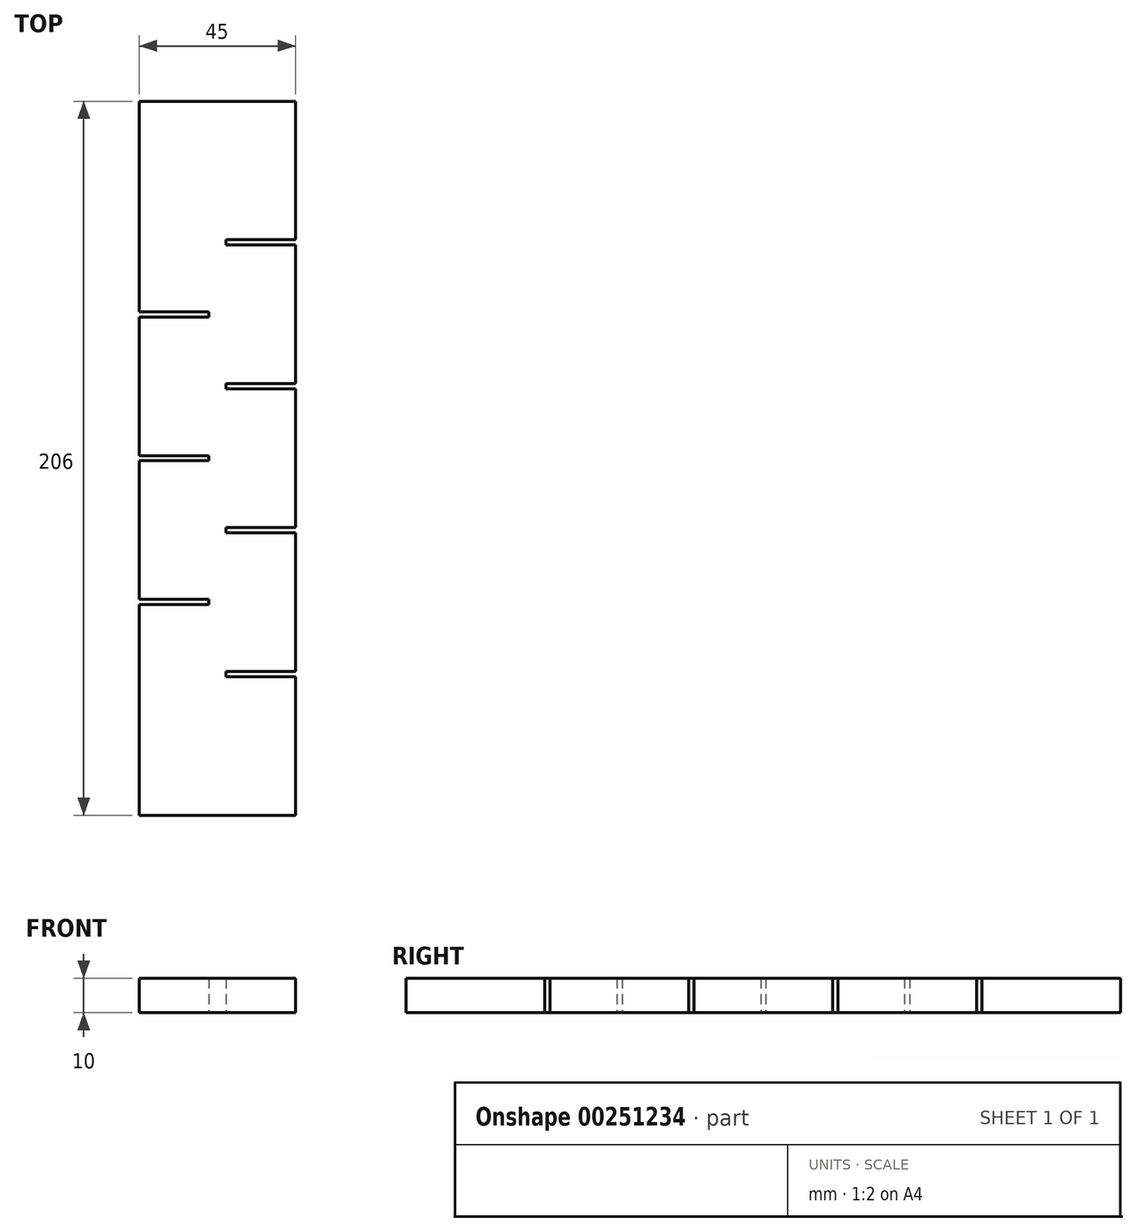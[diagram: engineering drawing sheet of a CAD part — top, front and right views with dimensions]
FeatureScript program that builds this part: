
annotation { "Feature Type Name" : "Feature", "Feature Type Description" : "" }
export const myFeature = defineFeature(function(context is Context, id is Id, definition is map)
    precondition{}
    {
        {
            var Q0;
            Q0=qCreatedBy(makeId("Top.planeOp"),FACE);
            var sketch = newSketch(context, id + "F0", { "sketchPlane" : qUnion([Q0])});
            skLineSegment(sketch, "E0", {"start": v(0, 0) * mm, "end": v(45, 0) * mm});
            skLineSegment(sketch, "E1", {"start": v(45, 0) * mm, "end": v(45, 40) * mm});
            skLineSegment(sketch, "E2", {"start": v(45, 40) * mm, "end": v(25, 40) * mm});
            skLineSegment(sketch, "E3", {"start": v(25, 40) * mm, "end": v(25, 41.5) * mm});
            skLineSegment(sketch, "E4", {"start": v(25, 41.5) * mm, "end": v(45, 41.5) * mm});
            skLineSegment(sketch, "E5", {"start": v(45, 41.5) * mm, "end": v(45, 81.5) * mm});
            skLineSegment(sketch, "E6", {"start": v(45, 81.5) * mm, "end": v(25, 81.5) * mm});
            skLineSegment(sketch, "E7", {"start": v(25, 81.5) * mm, "end": v(25, 83) * mm});
            skLineSegment(sketch, "E8", {"start": v(25, 83) * mm, "end": v(45, 83) * mm});
            skLineSegment(sketch, "E9", {"start": v(45, 83) * mm, "end": v(45, 123) * mm});
            skLineSegment(sketch, "E10", {"start": v(45, 123) * mm, "end": v(25, 123) * mm});
            skLineSegment(sketch, "E11", {"start": v(25, 123) * mm, "end": v(25, 124.5) * mm});
            skLineSegment(sketch, "E12", {"start": v(25, 124.5) * mm, "end": v(45, 124.5) * mm});
            skLineSegment(sketch, "E13", {"start": v(45, 124.5) * mm, "end": v(45, 164.5) * mm});
            skLineSegment(sketch, "E14", {"start": v(45, 164.5) * mm, "end": v(25, 164.5) * mm});
            skLineSegment(sketch, "E15", {"start": v(25, 164.5) * mm, "end": v(25, 166) * mm});
            skLineSegment(sketch, "E16", {"start": v(25, 166) * mm, "end": v(45, 166) * mm});
            skLineSegment(sketch, "E17", {"start": v(45, 166) * mm, "end": v(45, 206) * mm});
            skLineSegment(sketch, "E18", {"start": v(45, 206) * mm, "end": v(0, 206) * mm});
            skLineSegment(sketch, "E19", {"start": v(0, 206) * mm, "end": v(0, 145.25) * mm});
            skLineSegment(sketch, "E20", {"start": v(0, 145.25) * mm, "end": v(20, 145.25) * mm});
            skLineSegment(sketch, "E21", {"start": v(20, 145.25) * mm, "end": v(20, 143.75) * mm});
            skLineSegment(sketch, "E22", {"start": v(20, 143.75) * mm, "end": v(0, 143.75) * mm});
            skLineSegment(sketch, "E23", {"start": v(0, 143.75) * mm, "end": v(0, 103.75) * mm});
            skLineSegment(sketch, "E24", {"start": v(0, 103.75) * mm, "end": v(20, 103.75) * mm});
            skLineSegment(sketch, "E25", {"start": v(20, 103.75) * mm, "end": v(20, 102.25) * mm});
            skLineSegment(sketch, "E26", {"start": v(20, 102.25) * mm, "end": v(0, 102.25) * mm});
            skLineSegment(sketch, "E27", {"start": v(0, 102.25) * mm, "end": v(0, 62.25) * mm});
            skLineSegment(sketch, "E28", {"start": v(0, 62.25) * mm, "end": v(20, 62.25) * mm});
            skLineSegment(sketch, "E29", {"start": v(20, 62.25) * mm, "end": v(20, 60.75) * mm});
            skLineSegment(sketch, "E30", {"start": v(20, 60.75) * mm, "end": v(0, 60.75) * mm});
            skLineSegment(sketch, "E31", {"start": v(0, 60.75) * mm, "end": v(0, 0) * mm});
            skLineSegment(sketch, "E32", {"start": v(20, 144.5) * mm, "end": v(13.09, 144.5) * mm, "construction": true});
            skPoint(sketch, "E32.endSnap0", {"position": v(20, 144.5) * mm});
            skLineSegment(sketch, "E33", {"start": v(13.09, 144.5) * mm, "end": v(45, 144.5) * mm, "construction": true});
            skSolve(sketch);
        }
        {
            var Q0;
            Q0 = qSketchRegion(id + "F0", true);
            extrude(context, id + "F1", {"entities" : qUnion([Q0]), "depth" : 10 * mm});
        }
    });
